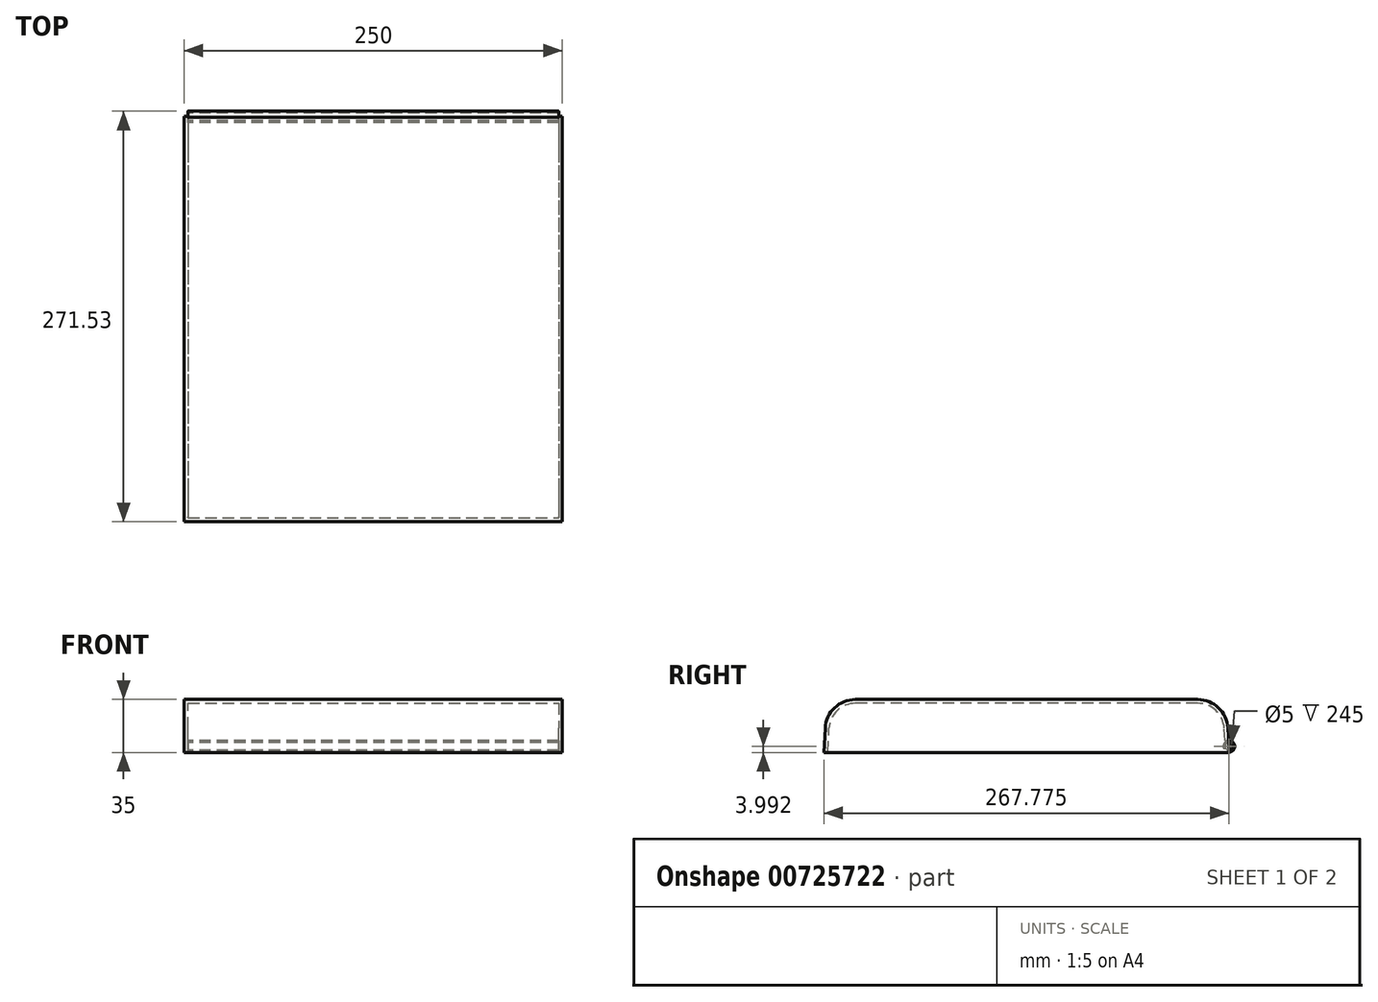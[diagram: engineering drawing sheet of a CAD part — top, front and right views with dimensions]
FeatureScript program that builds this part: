
annotation { "Feature Type Name" : "Feature", "Feature Type Description" : "" }
export const myFeature = defineFeature(function(context is Context, id is Id, definition is map)
    precondition{}
    {
        {
            var Q0;
            Q0=qCreatedBy(makeId("Right.planeOp"),FACE);
            var sketch = newSketch(context, id + "F0", { "sketchPlane" : qUnion([Q0])});
            skLineSegment(sketch, "E0.bottom", {"start": v(134, -19.06) * mm, "end": v(-134, -19.06) * mm});
            skLineSegment(sketch, "E0.top", {"start": v(113.12, 15.94) * mm, "end": v(-113.12, 15.94) * mm});
            skLineSegment(sketch, "E0.left", {"start": v(134, -19.06) * mm, "end": v(134, 25.94) * mm});
            skLineSegment(sketch, "E0.right", {"start": v(-134, -19.06) * mm, "end": v(-134, 25.94) * mm});
            skLineSegment(sketch, "E1", {"start": v(134, -19.06) * mm, "end": v(133.1, -2.94) * mm});
            skLineSegment(sketch, "E2", {"start": v(-134, -19.06) * mm, "end": v(-133.1, -2.94) * mm});
            skArc(sketch, "E3.filletArc", {"start": v(-113.12, 15.94) * mm, "mid": v(-126.86, 10.47) * mm, "end": v(-133.1, -2.94) * mm});
            skArc(sketch, "E4.filletArc", {"start": v(133.1, -2.94) * mm, "mid": v(126.86, 10.47) * mm, "end": v(113.12, 15.94) * mm});
            skSolve(sketch);
        }
        {
            var Q0;
            Q0=makeQuery(id+"F0.imprint","IMPRINT",FACE,{"disambiguationData":[TD([[makeQuery(id+"F0.imprint","IMPRINT",EDGE,{"derivedFrom":sQuery(id+"F0.wireOp",EDGE,"E0.bottom")}),-1.0]])]});
            extrude(context, id + "F1", {"entities" : qUnion([Q0]), "oppositeDirection" : true, "depth" : 250 * mm, "offsetDistance" : 25 * mm});
        }
        {
            var Q0;
            Q0=makeQuery(id+"F1.opExtrude","SWEPT_FACE",FACE,{"disambiguationData":[OSD([sQuery(id+"F0.wireOp",EDGE,"E0.bottom")])]});
            var Q1;
            Q1=makeQuery(id+"F1.opExtrude","SWEPT_BODY",BODY,{"disambiguationData":[OSD([sQuery(id+"F0.wireOp",EDGE,"E0.bottom"),sQuery(id+"F0.wireOp",EDGE,"E0.top"),sQuery(id+"F0.wireOp",EDGE,"E1"),sQuery(id+"F0.wireOp",EDGE,"E2"),sQuery(id+"F0.wireOp",EDGE,"E3.filletArc"),sQuery(id+"F0.wireOp",EDGE,"E4.filletArc")])]});
            shell(context, id + "F2", {"entities" : qUnion([Q0]), "parts" : qUnion([Q1]), "thickness" : 2.5 * mm});
        }
        {
            var Q0;
            Q0=makeQuery(id+"F1.opExtrude","SWEPT_FACE",FACE,{"disambiguationData":[OSD([sQuery(id+"F0.wireOp",EDGE,"E1")])]});
            var sketch = newSketch(context, id + "F3", { "sketchPlane" : qUnion([Q0])});
            skPoint(sketch, "E5.oppositeSnap0", {"position": v(0, -18.56) * mm});
            skLineSegment(sketch, "E5.bottom", {"start": v(2.5, -26.56) * mm, "end": v(247.5, -26.56) * mm});
            skLineSegment(sketch, "E5.top", {"start": v(2.5, -18.56) * mm, "end": v(247.5, -18.56) * mm});
            skLineSegment(sketch, "E5.left", {"start": v(2.5, -26.56) * mm, "end": v(2.5, -18.56) * mm});
            skLineSegment(sketch, "E5.right", {"start": v(247.5, -26.56) * mm, "end": v(247.5, -18.56) * mm});
            skSolve(sketch);
        }
        {
            var Q0;
            Q0=makeQuery(id+"F3.imprint","IMPRINT",FACE,{"disambiguationData":[TD([[makeQuery(id+"F3.imprint","IMPRINT",EDGE,{"derivedFrom":sQuery(id+"F3.wireOp",EDGE,"E5.bottom")}),-1.0]])]});
            extrude(context, id + "F4", {"entities" : qUnion([Q0]), "operationType" : NewBodyOperationType.REMOVE, "endBound" : BoundingType.THROUGH_ALL, "oppositeDirection" : true, "depth" : 25 * mm, "offsetDistance" : 25 * mm});
        }
        {
            var Q0;
            {var subQ0=sQuery(id+"F0.wireOp",EDGE,"E4.filletArc");var subQ1=sQuery(id+"F0.wireOp",EDGE,"E3.filletArc");var subQ2=sQuery(id+"F0.wireOp",EDGE,"E2");var subQ3=sQuery(id+"F0.wireOp",EDGE,"E1");var subQ4=sQuery(id+"F0.wireOp",EDGE,"E0.top");var subQ5=sQuery(id+"F0.wireOp",EDGE,"E0.bottom");Q0=makeQuery(id+"F4.boolean.opBoolean","MERGE",FACE,{"derivedFrom":[makeQuery(id+"F2.opShell","OFFSET_FACE",FACE,{"disambiguationData":[OSD([subQ5,subQ4,subQ3,subQ2,subQ1,subQ0]),TDD([makeQuery(id+"F1.opExtrude","CAP_FACE",FACE,{"disambiguationData":[OSD([subQ5,subQ4,subQ3,subQ2,subQ1,subQ0])],"isStart":false})])]}),makeQuery(id+"F4.opExtrude","SWEPT_FACE",FACE,{"disambiguationData":[OSD([sQuery(id+"F3.wireOp",EDGE,"E5.right")])]})]});}
            var sketch = newSketch(context, id + "F5", { "sketchPlane" : qUnion([Q0])});
            skCircle(sketch, "E6", {"center": v(133.78, -15.07) * mm, "radius": 3.75 * mm});
            skPoint(sketch, "E6.centerSnap0", {"position": v(131.05, -7.15) * mm});
            skCircle(sketch, "E7", {"center": v(133.78, -15.07) * mm, "radius": 2.5 * mm});
            skSolve(sketch);
        }
        {
            var Q0;
            {var subQ0=sQuery(id+"F5.wireOp",EDGE,"E6");var subQ1=makeQuery(id+"F4.boolean.opBoolean","COPY",EDGE,{"derivedFrom":makeQuery(id+"F4.opExtrude","CAP_EDGE",EDGE,{"disambiguationData":[OSD([sQuery(id+"F3.wireOp",EDGE,"E5.right")])],"isStart":true})});var subQ2=makeQuery(id+"F5.imprint","INTERSECT",VERTEX,{"disambiguationData":[OD(0.0)],"derivedFrom":[subQ1,subQ0]});Q0=makeQuery(id+"F5.imprint","IMPRINT",FACE,{"disambiguationData":[TD([[makeQuery(id+"F5.imprint","IMPRINT",EDGE,{"disambiguationData":[TD([[subQ2,1.0]])],"derivedFrom":subQ0}),1.0]])]});}
            var Q1;
            {var subQ0=sQuery(id+"F5.wireOp",EDGE,"E6");var subQ1=makeQuery(id+"F4.boolean.opBoolean","COPY",EDGE,{"derivedFrom":makeQuery(id+"F4.opExtrude","CAP_EDGE",EDGE,{"disambiguationData":[OSD([sQuery(id+"F3.wireOp",EDGE,"E5.right")])],"isStart":true})});var subQ2=makeQuery(id+"F5.imprint","INTERSECT",VERTEX,{"disambiguationData":[OD(0.0)],"derivedFrom":[subQ1,subQ0]});Q1=makeQuery(id+"F5.imprint","IMPRINT",FACE,{"disambiguationData":[TD([[makeQuery(id+"F5.imprint","IMPRINT",EDGE,{"disambiguationData":[TD([[subQ2,-1.0]])],"derivedFrom":subQ0}),1.0]])]});}
            extrude(context, id + "F6", {"entities" : qUnion([Q0, Q1]), "operationType" : NewBodyOperationType.ADD, "depth" : 245 * mm, "offsetDistance" : 25 * mm});
        }
    });
